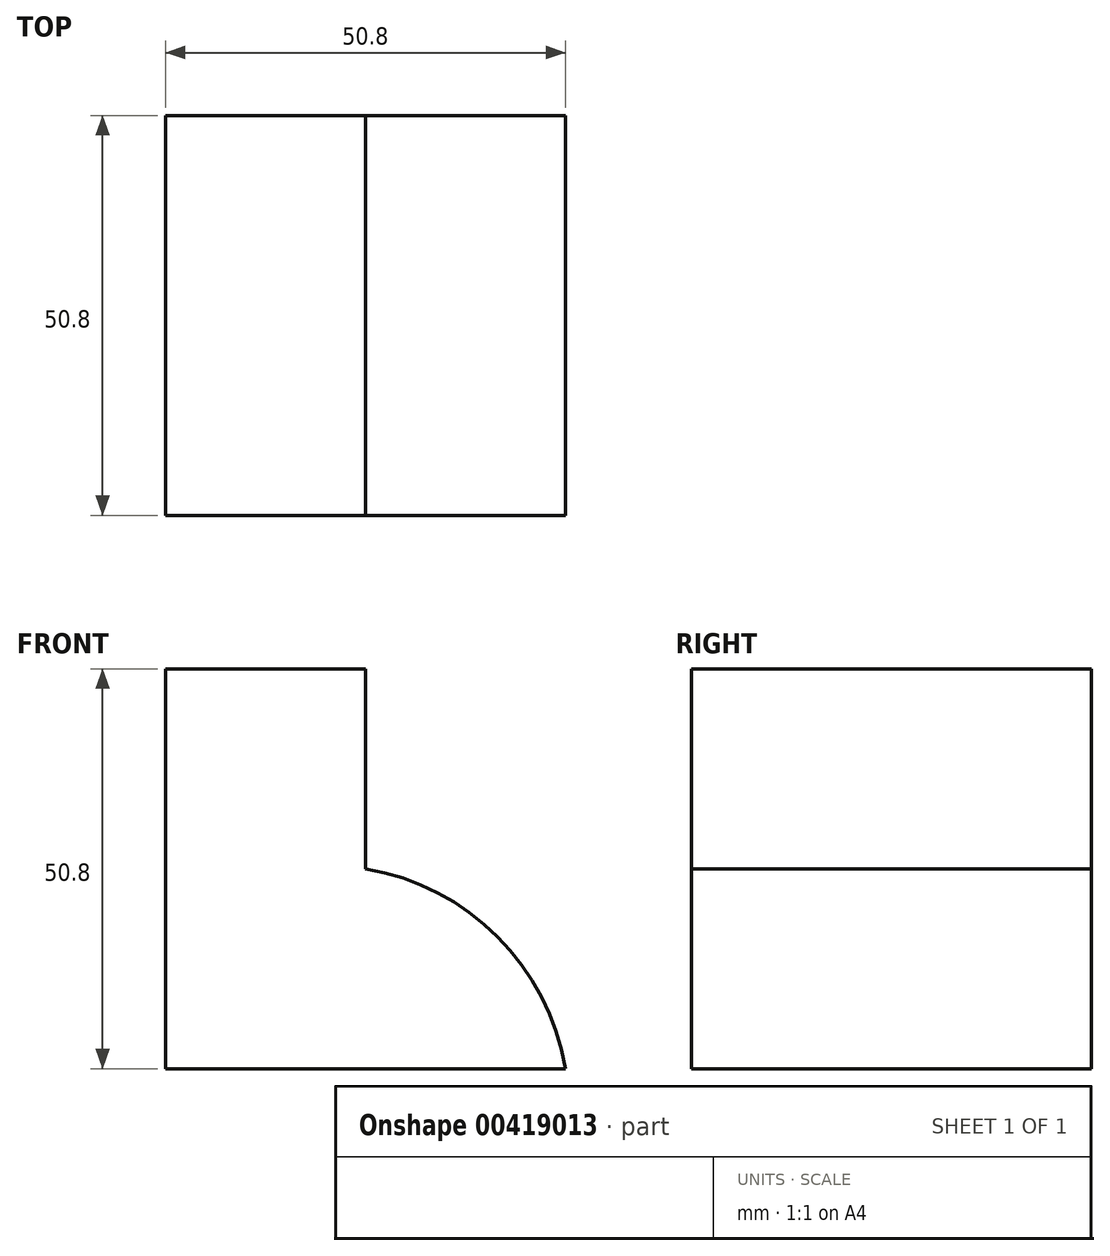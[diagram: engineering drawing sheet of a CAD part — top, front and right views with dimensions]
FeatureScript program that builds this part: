
annotation { "Feature Type Name" : "Feature", "Feature Type Description" : "" }
export const myFeature = defineFeature(function(context is Context, id is Id, definition is map)
    precondition{}
    {
        {
            var Q0;
            Q0=qCreatedBy(makeId("Front.planeOp"),FACE);
            var sketch = newSketch(context, id + "F0", { "sketchPlane" : qUnion([Q0])});
            skLineSegment(sketch, "E0", {"start": v(0, 0) * mm, "end": v(-50.8, 0) * mm});
            skLineSegment(sketch, "E1", {"start": v(-50.8, 0) * mm, "end": v(-50.8, 50.8) * mm});
            skLineSegment(sketch, "E2", {"start": v(-50.8, 50.8) * mm, "end": v(-25.4, 50.8) * mm});
            skLineSegment(sketch, "E3", {"start": v(-25.4, 50.8) * mm, "end": v(-25.4, 25.4) * mm});
            skArc(sketch, "E4", {"start": v(0, 0) * mm, "mid": v(-8.65, 16.75) * mm, "end": v(-25.4, 25.4) * mm});
            skSolve(sketch);
        }
        {
            var Q0;
            Q0 = qSketchRegion(id + "F0", true);
            extrude(context, id + "F1", {"entities" : qUnion([Q0]), "depth" : 50.8 * mm});
        }
    });
